# Revit family: BuzziTripl Home
name_source: partatom
category: Furniture
revit_build: Autodesk Revit 2018 (Build: 20190510_1515(x64)
units: mm (PartAtom-declared; Revit-internal decimal feet)

## family parameters
Always vertical = Yes
Cut with Voids When Loaded = No
OmniClass Number = 23.40.20.00
OmniClass Title = General Furniture and Specialties
Room Calculation Point = No
Shared = No
Work Plane-Based = No

## types (4) — shared parameters
Edge Material = <By Category>
Hinge Material = <By Category>
Panel Material = <By Category>

## per-type parameters (varying)
| type | Triple Home Type |
| BuzziTripl Home Low- Standard | Triple Home Low : Triple Home Low Standard |
| BuzziTripl Home Low- Zigzag | Triple Home Low : Triple Home Low Zigzag |
| BuzziTripl Home High- Standard | Triple Home High : Triple Home High Standard |
| BuzziTripl Home High- Zigzag | Triple Home High : Triple Home High Zigzag |

## geometry (parser evidence)
native form markers: Sweep x12
no freeform markers — native parametric forms only
